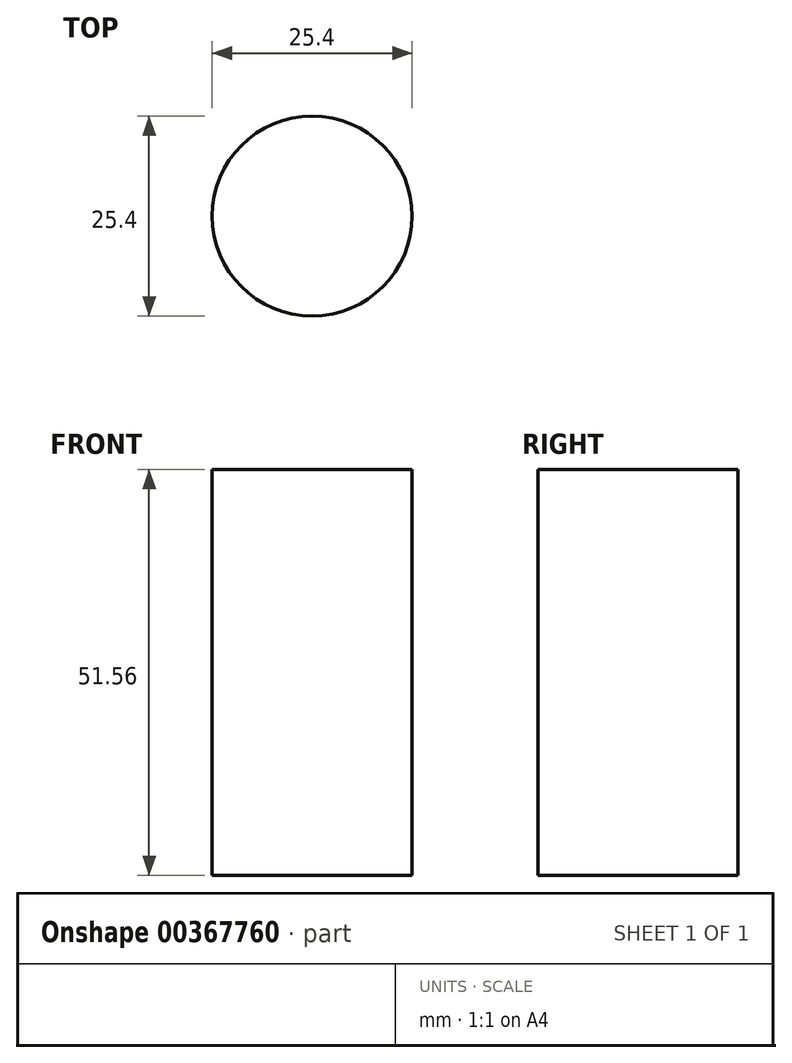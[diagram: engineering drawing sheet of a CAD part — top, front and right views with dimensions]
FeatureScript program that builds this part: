
annotation { "Feature Type Name" : "Feature", "Feature Type Description" : "" }
export const myFeature = defineFeature(function(context is Context, id is Id, definition is map)
    precondition{}
    {
        {
            var Q0;
            Q0=qCreatedBy(makeId("Top.planeOp"),FACE);
            var sketch = newSketch(context, id + "F0", { "sketchPlane" : qUnion([Q0])});
            skCircle(sketch, "E0", {"center": v(0, 0) * mm, "radius": 12.7 * mm});
            skSolve(sketch);
        }
        {
            var Q0;
            Q0=makeQuery(id+"F0.imprint","IMPRINT",FACE,{"disambiguationData":[TD([[makeQuery(id+"F0.imprint","IMPRINT",EDGE,{"derivedFrom":sQuery(id+"F0.wireOp",EDGE,"E0")}),1.0]])]});
            extrude(context, id + "F1", {"entities" : qUnion([Q0]), "depth" : 51.56 * mm});
        }
    });
